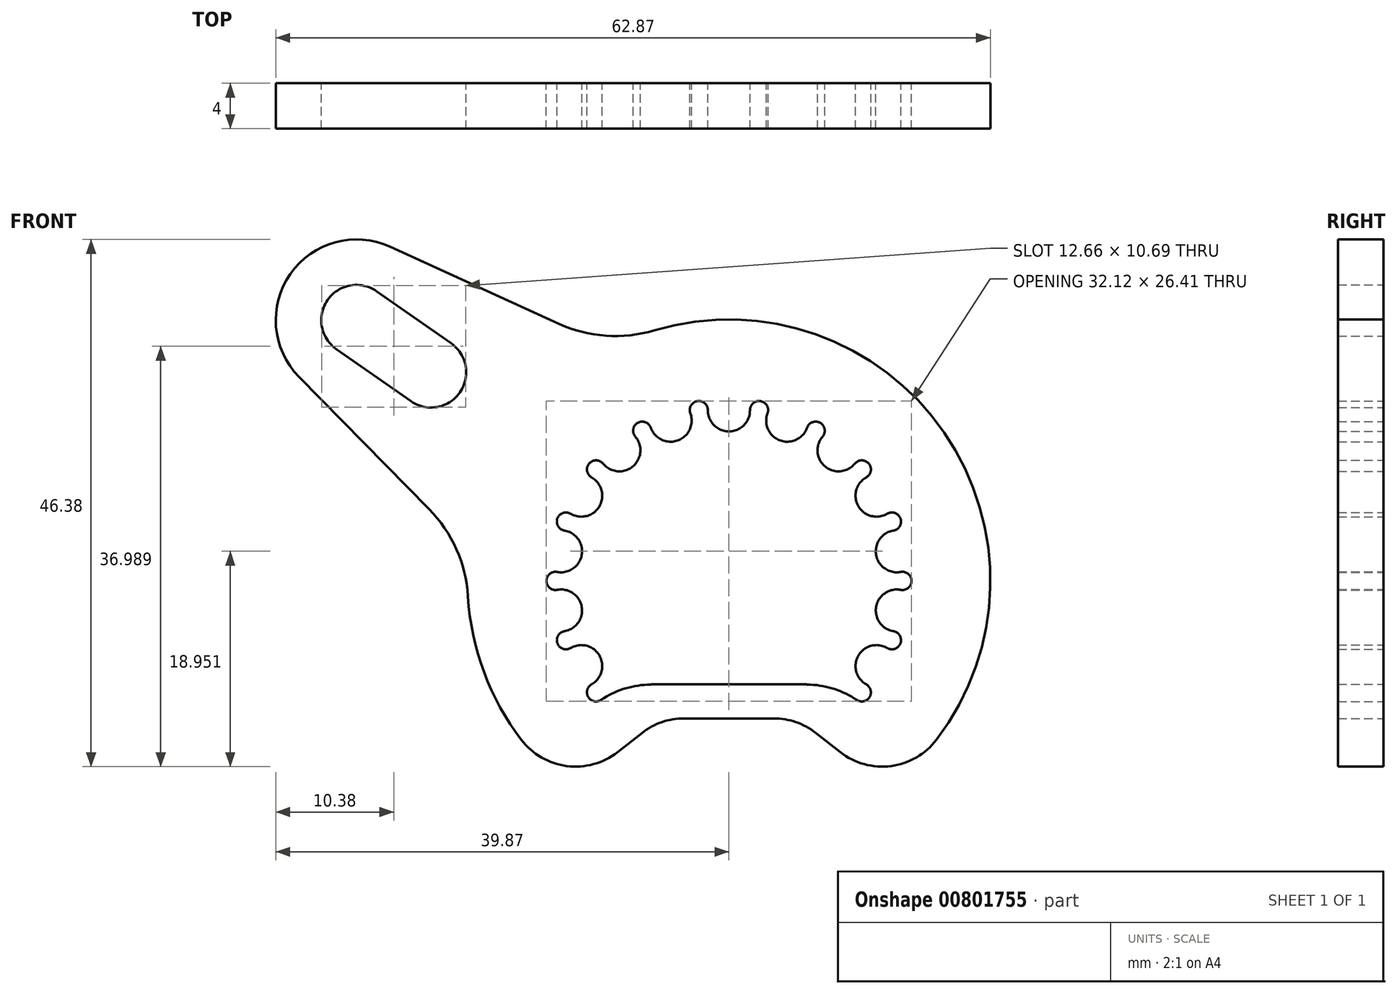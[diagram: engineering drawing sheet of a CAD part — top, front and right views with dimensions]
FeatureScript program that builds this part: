
annotation { "Feature Type Name" : "Feature", "Feature Type Description" : "" }
export const myFeature = defineFeature(function(context is Context, id is Id, definition is map)
    precondition{}
    {
        {
            var Q0;
            Q0=qCreatedBy(makeId("Front.planeOp"),FACE);
            var sketch = newSketch(context, id + "F0", { "sketchPlane" : qUnion([Q0])});
            skArc(sketch, "E0", {"start": v(-22.96, -1.37) * mm, "mid": v(-21.55, -8.03) * mm, "end": v(-18.26, -13.99) * mm});
            skLineSegment(sketch, "E1", {"start": v(-3.93, -12.1) * mm, "end": v(3.93, -12.1) * mm});
            skLineSegment(sketch, "E2", {"start": v(0, 0) * mm, "end": v(0, -12.1) * mm, "construction": true});
            skLineSegment(sketch, "E3", {"start": v(7.63, -13.37) * mm, "end": v(9.8, -15.07) * mm});
            skLineSegment(sketch, "E4", {"start": v(0, 0) * mm, "end": v(-32.77, 22.94) * mm, "construction": true});
            skLineSegment(sketch, "E5.trimOffspring", {"start": v(-28.05, 7.74) * mm, "end": v(-38.36, 14.96) * mm, "construction": true});
            skArc(sketch, "E6", {"start": v(-40.75, 28.54) * mm, "mid": v(-42.37, 21.25) * mm, "end": v(-38.36, 14.96) * mm, "construction": true});
            skArc(sketch, "E7.MirrorCS", {"start": v(-40.75, 28.54) * mm, "mid": v(-34.46, 32.54) * mm, "end": v(-27.17, 30.93) * mm, "construction": true});
            skLineSegment(sketch, "E8.MirrorCS", {"start": v(-16.87, 23.72) * mm, "end": v(-27.17, 30.93) * mm, "construction": true});
            skLineSegment(sketch, "E9.MirrorCS", {"start": v(-7.63, -13.37) * mm, "end": v(-9.8, -15.07) * mm});
            skArc(sketch, "E10.trimOffspring", {"start": v(18.26, -13.99) * mm, "mid": v(18.94, 13.05) * mm, "end": v(-6.56, 22.04) * mm});
            skLineSegment(sketch, "E11", {"start": v(-11.93, -9.1) * mm, "end": v(11.93, -9.1) * mm, "construction": true});
            skArc(sketch, "E12", {"start": v(11.43, -9.72) * mm, "mid": v(0, 15) * mm, "end": v(-11.43, -9.72) * mm, "construction": true});
            skPoint(sketch, "E13.visualSharp", {"position": v(-13.94, -18.3) * mm});
            skArc(sketch, "E13.filletArc", {"start": v(-18.26, -13.99) * mm, "mid": v(-14.25, -16.3) * mm, "end": v(-9.8, -15.07) * mm});
            skPoint(sketch, "E14.visualSharp", {"position": v(-6, -12.1) * mm});
            skArc(sketch, "E14.filletArc", {"start": v(-3.93, -12.1) * mm, "mid": v(-5.89, -12.42) * mm, "end": v(-7.63, -13.37) * mm});
            skPoint(sketch, "E15.visualSharp", {"position": v(6, -12.1) * mm});
            skArc(sketch, "E15.filletArc", {"start": v(7.63, -13.37) * mm, "mid": v(5.89, -12.42) * mm, "end": v(3.93, -12.1) * mm});
            skPoint(sketch, "E16.visualSharp", {"position": v(13.94, -18.3) * mm});
            skArc(sketch, "E16.filletArc", {"start": v(9.8, -15.07) * mm, "mid": v(14.25, -16.3) * mm, "end": v(18.26, -13.99) * mm});
            skPoint(sketch, "E17.visualSharp", {"position": v(-22.66, 3.96) * mm});
            skArc(sketch, "E17.filletArc", {"start": v(-22.96, -1.37) * mm, "mid": v(-24.46, 3.77) * mm, "end": v(-28.05, 7.74) * mm, "construction": true});
            skPoint(sketch, "E18.visualSharp", {"position": v(-11.47, 19.93) * mm});
            skArc(sketch, "E18.filletArc", {"start": v(-16.87, 23.72) * mm, "mid": v(-11.9, 21.7) * mm, "end": v(-6.56, 22.04) * mm});
            skArc(sketch, "E19", {"start": v(-30.99, 25.48) * mm, "mid": v(-35.3, 24.72) * mm, "end": v(-34.54, 20.4) * mm});
            skLineSegment(sketch, "E20", {"start": v(-28.43, -16.34) * mm, "end": v(42.41, -16.34) * mm, "construction": true});
            skLineSegment(sketch, "E21", {"start": v(-31.95, 22.37) * mm, "end": v(-26.35, 30.36) * mm, "construction": true});
            skArc(sketch, "E22", {"start": v(-24.72, 29.2) * mm, "mid": v(-26.21, 29.54) * mm, "end": v(-27.5, 28.72) * mm, "construction": true});
            skLineSegment(sketch, "E23", {"start": v(-32.8, 29.57) * mm, "end": v(-14.34, 29.57) * mm, "construction": true});
            skLineSegment(sketch, "E24", {"start": v(6, -12.1) * mm, "end": v(6, -9.1) * mm, "construction": true});
            skArc(sketch, "E25.trimOffspring", {"start": v(7.18, -9.13) * mm, "mid": v(6.6, -9.1) * mm, "end": v(6, -9.1) * mm});
            skArc(sketch, "E26.MirrorCS", {"start": v(-7.18, -9.13) * mm, "mid": v(-6.6, -9.1) * mm, "end": v(-6, -9.1) * mm});
            skLineSegment(sketch, "E27", {"start": v(-6, -9.1) * mm, "end": v(6, -9.1) * mm});
            skLineSegment(sketch, "E28", {"start": v(-34.54, 20.4) * mm, "end": v(-28, 15.82) * mm});
            skLineSegment(sketch, "E29", {"start": v(-30.99, 25.48) * mm, "end": v(-24.43, 20.9) * mm});
            skArc(sketch, "E30", {"start": v(-28, 15.82) * mm, "mid": v(-23.67, 16.58) * mm, "end": v(-24.43, 20.9) * mm});
            skArc(sketch, "E31.0", {"start": v(-29.82, 29.4) * mm, "mid": v(-38.58, 27.02) * mm, "end": v(-37.83, 17.96) * mm});
            skLineSegment(sketch, "E32", {"start": v(-37.83, 17.96) * mm, "end": v(-26.38, 6.33) * mm});
            skPoint(sketch, "E32.endSnap0", {"position": v(-24.46, 3.77) * mm});
            skPoint(sketch, "E33.orphan", {"position": v(-24.46, 4.38) * mm});
            skArc(sketch, "E34", {"start": v(-22.96, -1.37) * mm, "mid": v(-23.97, 2.79) * mm, "end": v(-26.38, 6.33) * mm});
            skLineSegment(sketch, "E35.MirrorCS", {"start": v(-29.82, 29.4) * mm, "end": v(-14.97, 22.63) * mm});
            skArc(sketch, "E36.MirrorCS", {"start": v(-6.56, 22.04) * mm, "mid": v(-10.82, 21.57) * mm, "end": v(-14.97, 22.63) * mm, "construction": true});
            skPoint(sketch, "E37.orphan", {"position": v(-16.87, 23.72) * mm});
            skLineSegment(sketch, "E38", {"start": v(0, 0) * mm, "end": v(13, -7.5) * mm, "construction": true});
            skArc(sketch, "E39", {"start": v(13.93, -5.9) * mm, "mid": v(11.39, -6.58) * mm, "end": v(12.08, -9.11) * mm});
            skLineSegment(sketch, "E40", {"start": v(0, 0) * mm, "end": v(14.77, -2.6) * mm, "construction": true});
            skArc(sketch, "E41", {"start": v(15.11, -0.79) * mm, "mid": v(12.95, -2.28) * mm, "end": v(14.47, -4.43) * mm});
            skArc(sketch, "E42", {"start": v(13.93, -5.9) * mm, "mid": v(15.1, -5.5) * mm, "end": v(14.47, -4.43) * mm});
            skArc(sketch, "E43", {"start": v(13.3, -5.67) * mm, "mid": v(14.17, -5.16) * mm, "end": v(13.83, -4.2) * mm, "construction": true});
            skArc(sketch, "E44.MirrorCS", {"start": v(12.08, -9.11) * mm, "mid": v(12.37, -10.23) * mm, "end": v(11.24, -10.47) * mm});
            skArc(sketch, "E45.MirrorCS", {"start": v(15.11, 0.79) * mm, "mid": v(16.06, 0) * mm, "end": v(15.11, -0.79) * mm});
            skPoint(sketch, "E46.orphan", {"position": v(11.07, -10.32) * mm});
            skPoint(sketch, "E47.visualSharp", {"position": v(10.92, -9.6) * mm});
            skArc(sketch, "E47.filletArc", {"start": v(11.24, -10.47) * mm, "mid": v(9.3, -9.52) * mm, "end": v(7.18, -9.13) * mm});
            skLineSegment(sketch, "E48", {"start": v(0, 0) * mm, "end": v(14.77, 2.6) * mm, "construction": true});
            skLineSegment(sketch, "E49", {"start": v(0, 0) * mm, "end": v(13, 7.5) * mm, "construction": true});
            skLineSegment(sketch, "E50", {"start": v(9.64, 11.5) * mm, "end": v(0, 0) * mm, "construction": true});
            skLineSegment(sketch, "E51", {"start": v(0, 0) * mm, "end": v(5.13, 14.1) * mm, "construction": true});
            skArc(sketch, "E52.MirrorCS", {"start": v(13.93, 5.9) * mm, "mid": v(11.39, 6.57) * mm, "end": v(12.08, 9.11) * mm});
            skArc(sketch, "E53.MirrorCS", {"start": v(14.47, 4.43) * mm, "mid": v(15.1, 5.5) * mm, "end": v(13.93, 5.9) * mm});
            skArc(sketch, "E54.MirrorCS", {"start": v(11.07, 10.32) * mm, "mid": v(12.3, 10.32) * mm, "end": v(12.08, 9.11) * mm});
            skArc(sketch, "E55.MirrorCS", {"start": v(11.07, 10.32) * mm, "mid": v(8.45, 10.07) * mm, "end": v(8.24, 12.7) * mm});
            skArc(sketch, "E56.MirrorCS", {"start": v(15.11, 0.79) * mm, "mid": v(12.95, 2.28) * mm, "end": v(14.47, 4.43) * mm});
            skArc(sketch, "E57.MirrorCS", {"start": v(8.24, 12.7) * mm, "mid": v(8.03, 13.9) * mm, "end": v(6.88, 13.48) * mm});
            skArc(sketch, "E58.MirrorCS", {"start": v(3.4, 14.75) * mm, "mid": v(4.5, 12.36) * mm, "end": v(6.88, 13.48) * mm});
            skArc(sketch, "E59.MirrorCS", {"start": v(1.85, 15.02) * mm, "mid": v(2.79, 15.82) * mm, "end": v(3.4, 14.75) * mm});
            skArc(sketch, "E60.MirrorCS", {"start": v(-1.85, 15.02) * mm, "mid": v(0, 13.15) * mm, "end": v(1.85, 15.02) * mm});
            skArc(sketch, "E61.MirrorCS", {"start": v(-1.85, 15.02) * mm, "mid": v(-2.79, 15.82) * mm, "end": v(-3.4, 14.75) * mm});
            skArc(sketch, "E62.MirrorCS", {"start": v(-3.4, 14.75) * mm, "mid": v(-4.5, 12.36) * mm, "end": v(-6.88, 13.48) * mm});
            skArc(sketch, "E63.MirrorCS", {"start": v(-8.24, 12.7) * mm, "mid": v(-8.03, 13.9) * mm, "end": v(-6.88, 13.48) * mm});
            skArc(sketch, "E64.MirrorCS", {"start": v(-11.07, 10.32) * mm, "mid": v(-8.45, 10.07) * mm, "end": v(-8.24, 12.7) * mm});
            skArc(sketch, "E65.MirrorCS", {"start": v(-11.07, 10.32) * mm, "mid": v(-12.3, 10.32) * mm, "end": v(-12.08, 9.11) * mm});
            skArc(sketch, "E66.MirrorCS", {"start": v(-13.93, 5.9) * mm, "mid": v(-11.39, 6.57) * mm, "end": v(-12.08, 9.11) * mm});
            skArc(sketch, "E67.MirrorCS", {"start": v(-14.47, 4.43) * mm, "mid": v(-15.1, 5.5) * mm, "end": v(-13.93, 5.9) * mm});
            skArc(sketch, "E68.MirrorCS", {"start": v(-15.11, 0.79) * mm, "mid": v(-12.95, 2.28) * mm, "end": v(-14.47, 4.43) * mm});
            skArc(sketch, "E69.MirrorCS", {"start": v(-15.11, 0.79) * mm, "mid": v(-16.06, 0) * mm, "end": v(-15.11, -0.79) * mm});
            skArc(sketch, "E70.MirrorCS", {"start": v(-15.11, -0.79) * mm, "mid": v(-12.95, -2.28) * mm, "end": v(-14.47, -4.43) * mm});
            skArc(sketch, "E71.MirrorCS", {"start": v(-13.93, -5.9) * mm, "mid": v(-15.1, -5.5) * mm, "end": v(-14.47, -4.43) * mm});
            skArc(sketch, "E72.MirrorCS", {"start": v(-13.93, -5.9) * mm, "mid": v(-11.39, -6.58) * mm, "end": v(-12.08, -9.11) * mm});
            skArc(sketch, "E73.MirrorCS", {"start": v(-12.08, -9.11) * mm, "mid": v(-12.37, -10.23) * mm, "end": v(-11.24, -10.47) * mm});
            skArc(sketch, "E74.MirrorCS", {"start": v(-11.24, -10.47) * mm, "mid": v(-9.3, -9.52) * mm, "end": v(-7.18, -9.13) * mm});
            skPoint(sketch, "E75.orphan", {"position": v(-11.43, -9.72) * mm});
            skSolve(sketch);
        }
        {
            var Q0;
            Q0=makeQuery(id+"F0.imprint","IMPRINT",FACE,{"disambiguationData":[TD([[makeQuery(id+"F0.imprint","IMPRINT",EDGE,{"derivedFrom":sQuery(id+"F0.wireOp",EDGE,"E0")}),1.0]])]});
            extrude(context, id + "F1", {"entities" : qUnion([Q0]), "depth" : 4 * mm, "offsetDistance" : 25 * mm});
        }
    });
